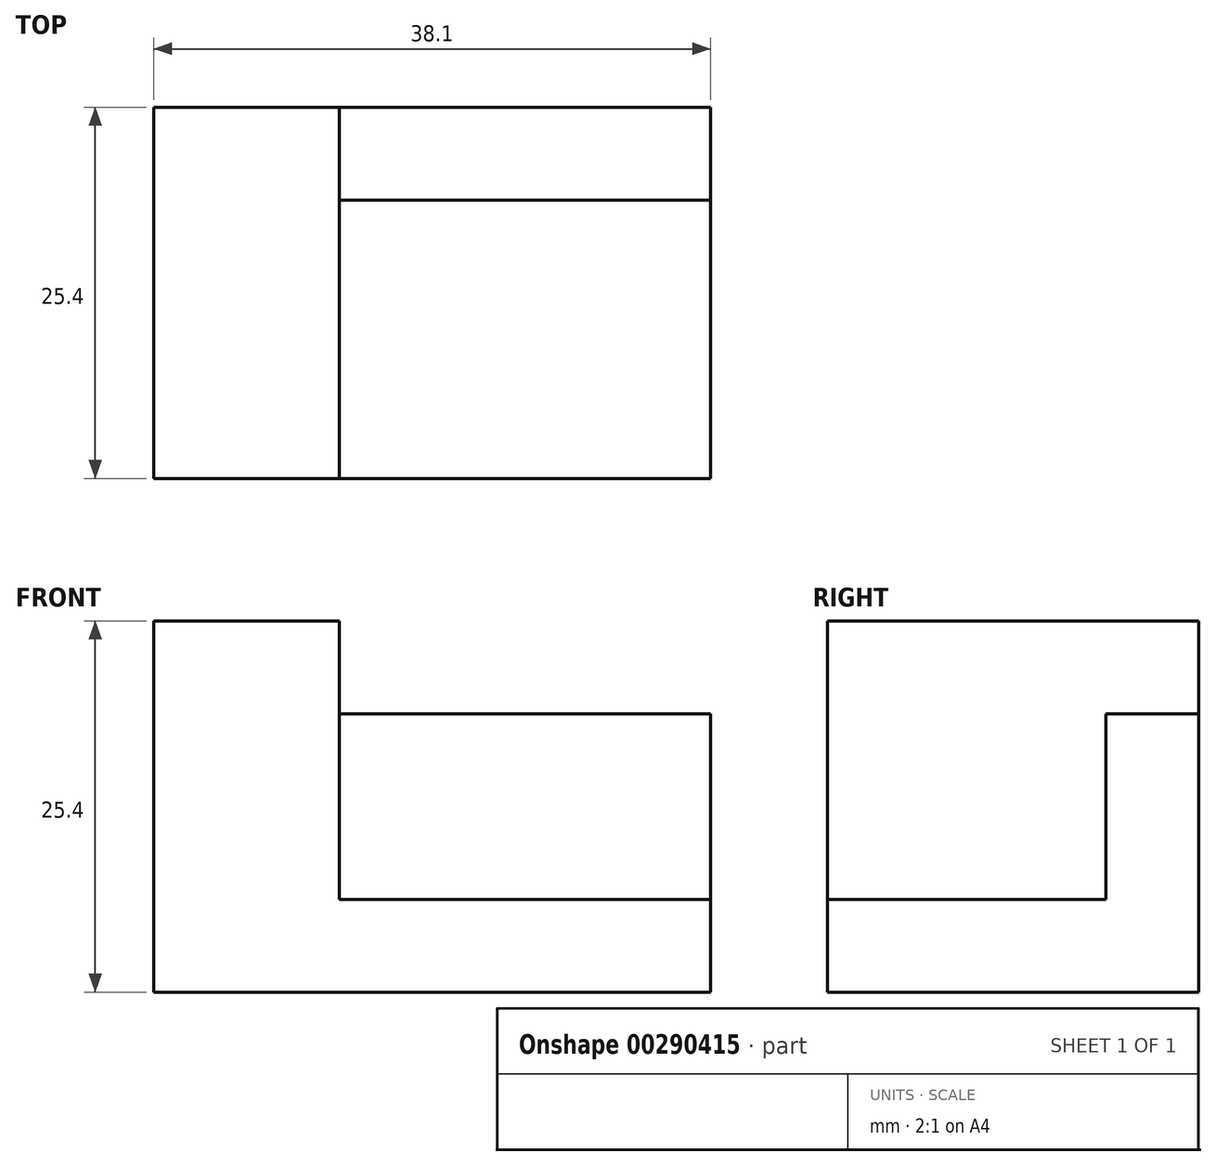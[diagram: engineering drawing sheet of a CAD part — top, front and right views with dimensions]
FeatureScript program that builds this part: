
annotation { "Feature Type Name" : "Feature", "Feature Type Description" : "" }
export const myFeature = defineFeature(function(context is Context, id is Id, definition is map)
    precondition{}
    {
        {
            var Q0;
            Q0=qCreatedBy(makeId("Top.planeOp"),FACE);
            var sketch = newSketch(context, id + "F0", { "sketchPlane" : qUnion([Q0])});
            skLineSegment(sketch, "E0.bottom", {"start": v(-33.27, 0) * mm, "end": v(4.83, 0) * mm});
            skLineSegment(sketch, "E0.top", {"start": v(-33.27, 25.4) * mm, "end": v(4.83, 25.4) * mm});
            skLineSegment(sketch, "E0.left", {"start": v(-33.27, 0) * mm, "end": v(-33.27, 25.4) * mm});
            skLineSegment(sketch, "E0.right", {"start": v(4.83, 0) * mm, "end": v(4.83, 25.4) * mm});
            skSolve(sketch);
        }
        {
            var Q0;
            Q0 = qSketchRegion(id + "F0", true);
            extrude(context, id + "F1", {"entities" : qUnion([Q0]), "depth" : 6.35 * mm});
        }
        {
            var Q0;
            Q0=makeQuery(id+"F1.opExtrude","CAP_FACE",FACE,{"disambiguationData":[OSD([sQuery(id+"F0.wireOp",EDGE,"E0.bottom"),sQuery(id+"F0.wireOp",EDGE,"E0.top"),sQuery(id+"F0.wireOp",EDGE,"E0.left"),sQuery(id+"F0.wireOp",EDGE,"E0.right")])],"isStart":false});
            var sketch = newSketch(context, id + "F2", { "sketchPlane" : qUnion([Q0])});
            skLineSegment(sketch, "E1", {"start": v(-20.57, 25.4) * mm, "end": v(-20.57, 0) * mm});
            skLineSegment(sketch, "E2", {"start": v(-20.57, 19.05) * mm, "end": v(4.83, 19.05) * mm});
            skSolve(sketch);
        }
        {
            var Q0;
            Q0 = qSketchRegion(id + "F2", true);
            var Q1;
            {var subQ0=makeQuery(id+"F1.opExtrude","CAP_EDGE",EDGE,{"disambiguationData":[OSD([sQuery(id+"F0.wireOp",EDGE,"E0.left")])],"isStart":false});Q1=makeQuery(id+"F2.imprint","IMPRINT",FACE,{"disambiguationData":[TD([[makeQuery(id+"F2.imprint","IMPRINT",EDGE,{"derivedFrom":subQ0}),-1.0]])]});}
            extrude(context, id + "F3", {"entities" : qUnion([Q0, Q1]), "operationType" : NewBodyOperationType.ADD, "depth" : 19.05 * mm});
        }
        {
            var Q0;
            Q0=makeQuery(id+"F1.opExtrude","CAP_FACE",FACE,{"disambiguationData":[OSD([sQuery(id+"F0.wireOp",EDGE,"E0.bottom"),sQuery(id+"F0.wireOp",EDGE,"E0.top"),sQuery(id+"F0.wireOp",EDGE,"E0.left"),sQuery(id+"F0.wireOp",EDGE,"E0.right")])],"isStart":false});
            var sketch = newSketch(context, id + "F4", { "sketchPlane" : qUnion([Q0])});
            skLineSegment(sketch, "E3", {"start": v(-20.57, 19.05) * mm, "end": v(4.83, 19.05) * mm});
            skSolve(sketch);
        }
        {
            var Q0;
            Q0 = qSketchRegion(id + "F4", true);
            var Q1;
            {var subQ0=sQuery(id+"F4.wireOp",EDGE,"E3");Q1=makeQuery(id+"F4.imprint","IMPRINT",FACE,{"disambiguationData":[TD([[makeQuery(id+"F4.imprint","IMPRINT",EDGE,{"derivedFrom":subQ0}),1.0]])]});}
            extrude(context, id + "F5", {"entities" : qUnion([Q0, Q1]), "operationType" : NewBodyOperationType.ADD, "depth" : 12.7 * mm});
        }
    });
